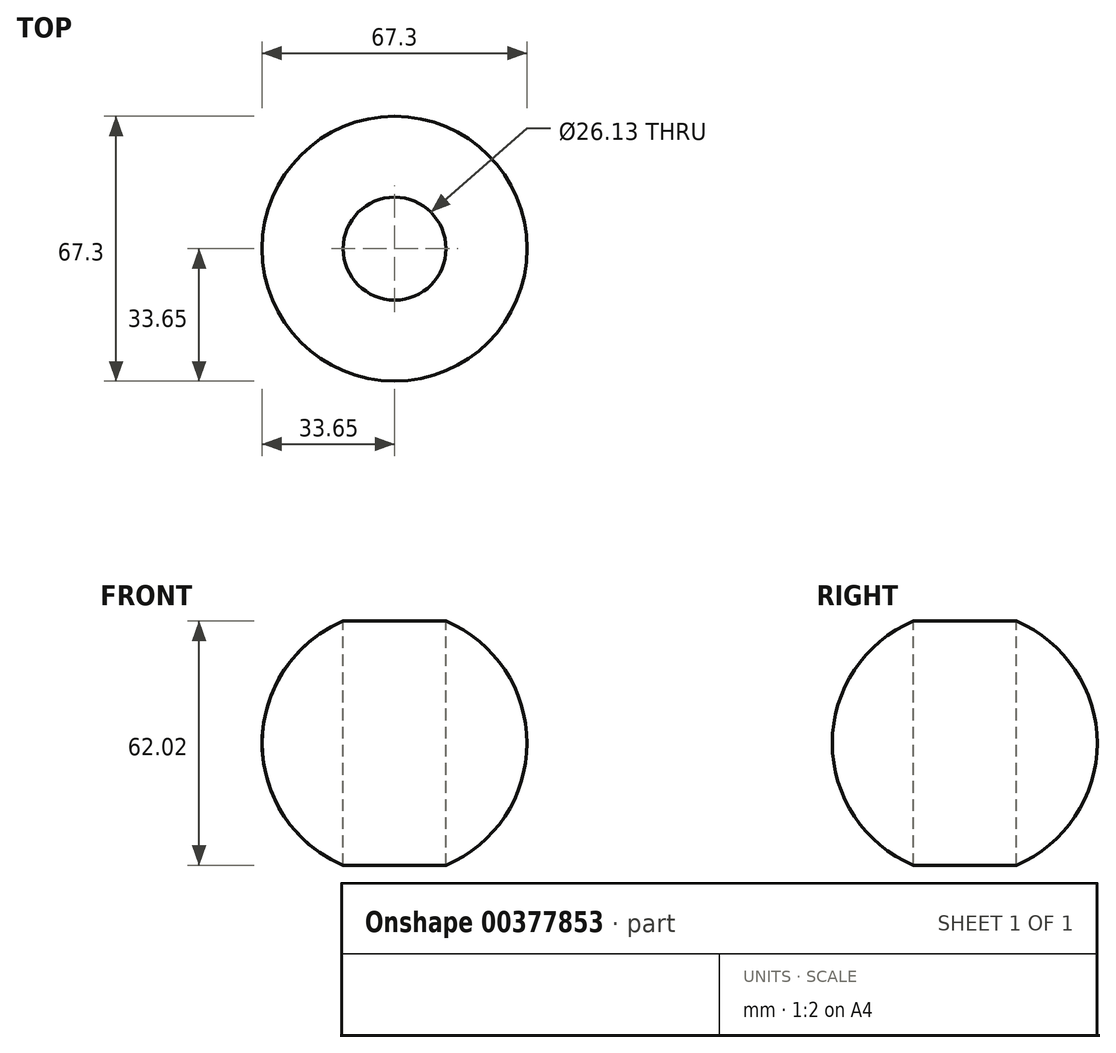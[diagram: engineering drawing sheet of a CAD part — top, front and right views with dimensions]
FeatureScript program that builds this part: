
annotation { "Feature Type Name" : "Feature", "Feature Type Description" : "" }
export const myFeature = defineFeature(function(context is Context, id is Id, definition is map)
    precondition{}
    {
        {
            var Q0;
            Q0=qCreatedBy(makeId("Front.planeOp"),FACE);
            var sketch = newSketch(context, id + "F0", { "sketchPlane" : qUnion([Q0])});
            skArc(sketch, "E0", {"start": v(0, 33.65) * mm, "mid": v(-33.65, 0) * mm, "end": v(0, -33.65) * mm});
            skLineSegment(sketch, "E1", {"start": v(0, 42.89) * mm, "end": v(0, -45.62) * mm, "construction": true});
            skLineSegment(sketch, "E2", {"start": v(0, 33.65) * mm, "end": v(0, -33.65) * mm});
            skSolve(sketch);
        }
        {
            var Q0;
            Q0=makeQuery(id+"F0.imprint","IMPRINT",FACE,{"disambiguationData":[TD([[makeQuery(id+"F0.imprint","IMPRINT",EDGE,{"derivedFrom":sQuery(id+"F0.wireOp",EDGE,"E0")}),1.0]])]});
            var Q1;
            Q1=sQuery(id+"F0.wireOp",EDGE,"E1");
            revolve(context, id + "F1", {"entities" : qUnion([Q0]), "axis" : qUnion([Q1]), "revolveType" : RevolveType.FULL});
        }
        {
            var Q0;
            Q0=qCreatedBy(makeId("Top.planeOp"),FACE);
            cPlane(context, id + "F2", {"entities" : qUnion([Q0]), "cplaneType" : CPlaneType.OFFSET, "offset" : 127 * mm, "width" : 152.4 * mm, "height" : 152.4 * mm});
        }
        {
            var Q0;
            Q0=qCreatedBy(id+"F2.planeOp",FACE);
            var sketch = newSketch(context, id + "F3", { "sketchPlane" : qUnion([Q0])});
            skCircle(sketch, "E3", {"center": v(0, 0) * mm, "radius": 13.06 * mm});
            skSolve(sketch);
        }
        {
            var Q0;
            Q0=makeQuery(id+"F3.imprint","IMPRINT",FACE,{"disambiguationData":[TD([[makeQuery(id+"F3.imprint","IMPRINT",EDGE,{"derivedFrom":sQuery(id+"F3.wireOp",EDGE,"E3")}),1.0]])]});
            var Q1;
            Q1=sQuery(id+"F3.wireOp",EDGE,"E3");
            extrude(context, id + "F4", {"entities" : qUnion([Q0]), "operationType" : NewBodyOperationType.REMOVE, "surfaceEntities" : qUnion([Q1]), "oppositeDirection" : true, "depth" : 381 * mm});
        }
    });
